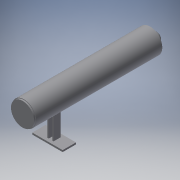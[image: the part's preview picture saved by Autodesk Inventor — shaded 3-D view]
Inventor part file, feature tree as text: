
AUTODESK INVENTOR PART (.ipt)
format: ipt  version: 2018.3 (Build 223284000, 284)  size: 199,680 bytes
history: native  units: mm
features: extrude x9, sketch x8, chamfer x2, fillet x2
ambient origin geometry x8: Origin, YZ Plane, XZ Plane, XY Plane, X Axis, Y Axis, Z Axis, Center Point
bodies: Solid1 (feature_tree)
feature tree (21):
  extrude  "Extrusion1"  Depth=12.5mm
  extrude  "Extrusion2"  Depth=0.7mm TaperAngle=0.0deg
  extrude  "Extrusion4"  Depth=3.0mm
  extrude  "Extrusion15"  Depth=1.25mm
  extrude  "Extrusion16"  Depth=1.5mm
  chamfer  "Chamfer4"  Distance=10.0mm
  extrude  "Extrusion17"  Depth=1.5mm
  chamfer  "Chamfer5"  Distance=40.0mm
  extrude  "Extrusion18"  Depth=1.5mm
  fillet  "Fillet4"  Radius=10.0mm
  fillet  "Fillet5"  Radius=1.0mm
  extrude  "Extrusion19"  Depth=4.9mm TaperAngle=45.0deg
  extrude  "Extrusion20"  Depth=1.5mm TaperAngle=0.0deg
  sketch  "Sketch2"  dims[d0=1.8mm d2=12.5mm]
  sketch  "Sketch4"  dims[d3=5.5mm d6=0.7mm d7=0.0mm]
  sketch  "Sketch15"  dims[d8=0.5mm d9=3.0mm]
  sketch  "Sketch16"  dims[d10=0.5mm d11=1.25mm]
  sketch  "Sketch17"  dims[d12=1.25mm d13=1.5mm]
  sketch  "Sketch18"  dims[d14=5.0mm]
  sketch  "Sketch19"  dims[d15=5.0mm d16=10.0mm d17=0.0mm]
  sketch  "Sketch20"  dims[d35=10.0mm d36=14.8mm d37=40.0mm d38=0.0mm d70=9.8mm d71=10.0mm d72=0.0mm d73=1.0mm d74=0.0mm d75=4.9mm d76=2.0mm d77=45.0deg d78=1.0mm d79=0.0mm d80=4.9mm d81=2.0mm d82=45.0deg d83=4.8mm d84=3.0mm d85=0.0mm d86=1.5mm d87=1.5mm d88=0.1mm d89=0.0mm d90=0.5mm d91=0.0mm]
